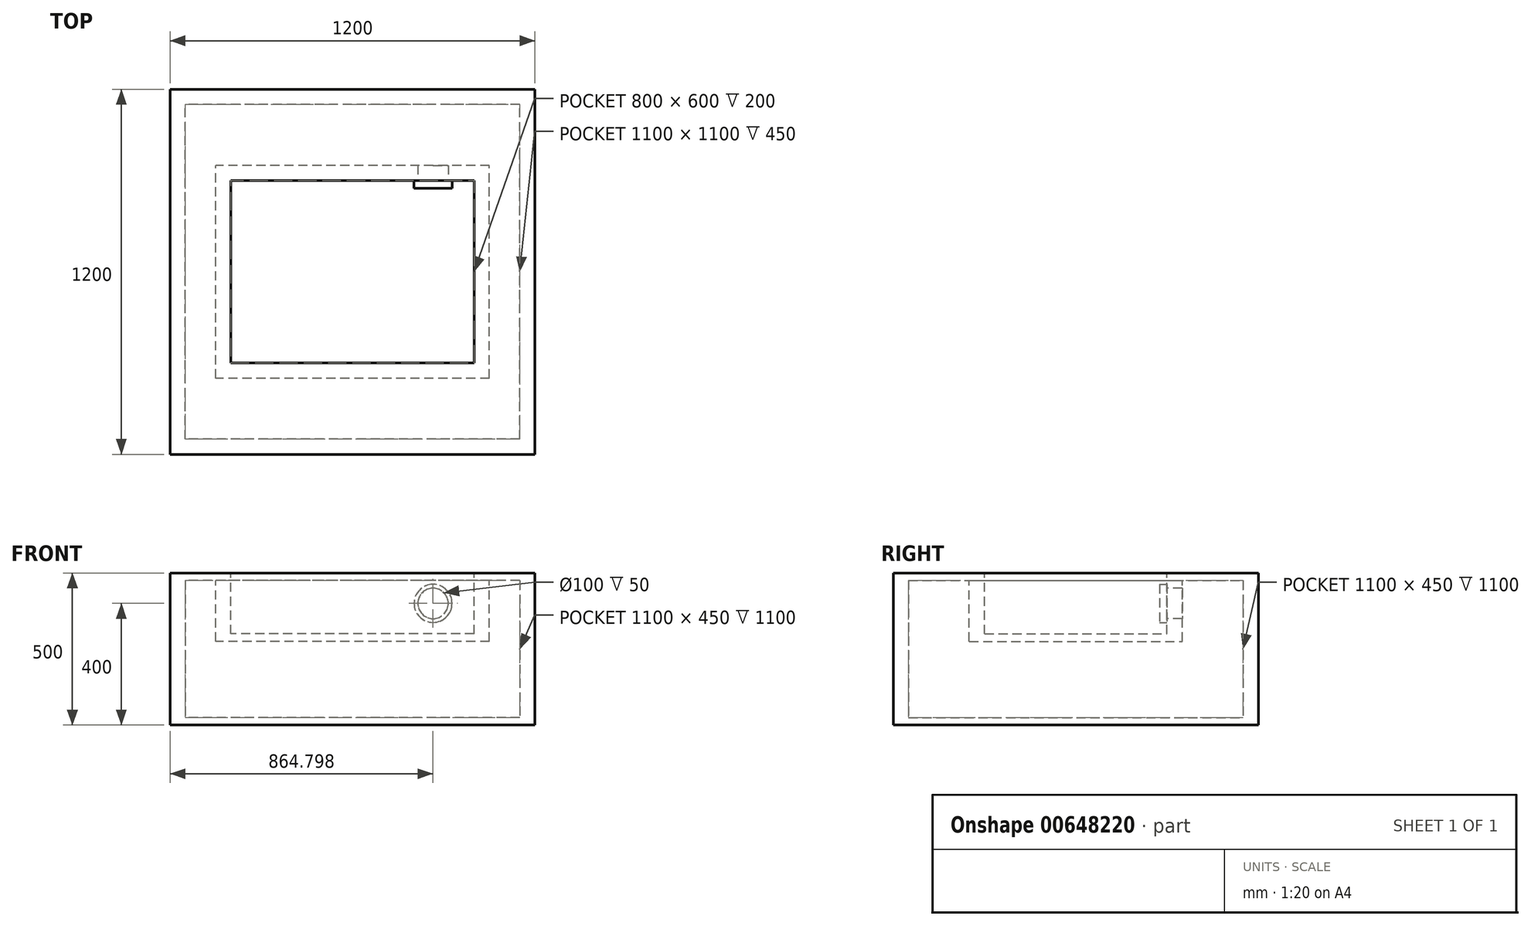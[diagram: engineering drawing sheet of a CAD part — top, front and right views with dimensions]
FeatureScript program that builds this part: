
annotation { "Feature Type Name" : "Feature", "Feature Type Description" : "" }
export const myFeature = defineFeature(function(context is Context, id is Id, definition is map)
    precondition{}
    {
        {
            var Q0;
            Q0=qCreatedBy(makeId("Top.planeOp"),FACE);
            var sketch = newSketch(context, id + "F0", { "sketchPlane" : qUnion([Q0])});
            skLineSegment(sketch, "E0.bottom", {"start": v(150, 150) * mm, "end": v(-150, 150) * mm, "construction": true});
            skLineSegment(sketch, "E0.top", {"start": v(150, -150) * mm, "end": v(-150, -150) * mm, "construction": true});
            skLineSegment(sketch, "E0.left", {"start": v(150, 150) * mm, "end": v(150, -150) * mm, "construction": true});
            skLineSegment(sketch, "E0.right", {"start": v(-150, 150) * mm, "end": v(-150, -150) * mm, "construction": true});
            skPoint(sketch, "E0.middle", {"position": v(0, 0) * mm});
            skPoint(sketch, "E1.0.1.0", {"position": v(0, 325) * mm});
            skLineSegment(sketch, "E1.0.1.1", {"start": v(-150, 475) * mm, "end": v(-150, 175) * mm, "construction": true});
            skLineSegment(sketch, "E1.0.1.2", {"start": v(150, 475) * mm, "end": v(150, 175) * mm, "construction": true});
            skLineSegment(sketch, "E1.0.1.3", {"start": v(150, 175) * mm, "end": v(-150, 175) * mm, "construction": true});
            skLineSegment(sketch, "E1.0.1.4", {"start": v(150, 475) * mm, "end": v(-150, 475) * mm, "construction": true});
            skLineSegment(sketch, "E1.0.2.1", {"start": v(-150, 800) * mm, "end": v(-150, 500) * mm, "construction": true});
            skLineSegment(sketch, "E1.0.2.2", {"start": v(150, 800) * mm, "end": v(150, 500) * mm, "construction": true});
            skLineSegment(sketch, "E1.0.2.3", {"start": v(150, 500) * mm, "end": v(-150, 500) * mm, "construction": true});
            skLineSegment(sketch, "E1.0.2.4", {"start": v(150, 800) * mm, "end": v(-150, 800) * mm, "construction": true});
            skPoint(sketch, "E1.1.0.0", {"position": v(325, 0) * mm});
            skLineSegment(sketch, "E1.1.0.1", {"start": v(175, 150) * mm, "end": v(175, -150) * mm, "construction": true});
            skLineSegment(sketch, "E1.1.0.2", {"start": v(475, 150) * mm, "end": v(475, -150) * mm, "construction": true});
            skLineSegment(sketch, "E1.1.0.3", {"start": v(475, -150) * mm, "end": v(175, -150) * mm, "construction": true});
            skLineSegment(sketch, "E1.1.0.4", {"start": v(475, 150) * mm, "end": v(175, 150) * mm, "construction": true});
            skPoint(sketch, "E1.1.1.0", {"position": v(325, 325) * mm});
            skLineSegment(sketch, "E1.1.1.1", {"start": v(175, 475) * mm, "end": v(175, 175) * mm, "construction": true});
            skLineSegment(sketch, "E1.1.1.2", {"start": v(475, 475) * mm, "end": v(475, 175) * mm, "construction": true});
            skLineSegment(sketch, "E1.1.1.3", {"start": v(475, 175) * mm, "end": v(175, 175) * mm, "construction": true});
            skLineSegment(sketch, "E1.1.1.4", {"start": v(475, 475) * mm, "end": v(175, 475) * mm, "construction": true});
            skPoint(sketch, "E1.1.2.0", {"position": v(325, 650) * mm});
            skLineSegment(sketch, "E1.1.2.1", {"start": v(175, 800) * mm, "end": v(175, 500) * mm, "construction": true});
            skLineSegment(sketch, "E1.1.2.2", {"start": v(475, 800) * mm, "end": v(475, 500) * mm, "construction": true});
            skLineSegment(sketch, "E1.1.2.3", {"start": v(475, 500) * mm, "end": v(175, 500) * mm, "construction": true});
            skLineSegment(sketch, "E1.1.2.4", {"start": v(475, 800) * mm, "end": v(175, 800) * mm, "construction": true});
            skLineSegment(sketch, "E1.2.0.1", {"start": v(500, 150) * mm, "end": v(500, -150) * mm, "construction": true});
            skLineSegment(sketch, "E1.2.0.2", {"start": v(800, 150) * mm, "end": v(800, -150) * mm, "construction": true});
            skLineSegment(sketch, "E1.2.0.3", {"start": v(800, -150) * mm, "end": v(500, -150) * mm, "construction": true});
            skLineSegment(sketch, "E1.2.0.4", {"start": v(800, 150) * mm, "end": v(500, 150) * mm, "construction": true});
            skPoint(sketch, "E1.2.1.0", {"position": v(650, 325) * mm});
            skLineSegment(sketch, "E1.2.1.1", {"start": v(500, 475) * mm, "end": v(500, 175) * mm, "construction": true});
            skLineSegment(sketch, "E1.2.1.2", {"start": v(800, 475) * mm, "end": v(800, 175) * mm, "construction": true});
            skLineSegment(sketch, "E1.2.1.3", {"start": v(800, 175) * mm, "end": v(500, 175) * mm, "construction": true});
            skLineSegment(sketch, "E1.2.1.4", {"start": v(800, 475) * mm, "end": v(500, 475) * mm, "construction": true});
            skLineSegment(sketch, "E1.2.2.1", {"start": v(500, 800) * mm, "end": v(500, 500) * mm, "construction": true});
            skLineSegment(sketch, "E1.2.2.2", {"start": v(800, 800) * mm, "end": v(800, 500) * mm, "construction": true});
            skLineSegment(sketch, "E1.2.2.3", {"start": v(800, 500) * mm, "end": v(500, 500) * mm, "construction": true});
            skLineSegment(sketch, "E1.2.2.4", {"start": v(800, 800) * mm, "end": v(500, 800) * mm, "construction": true});
            skLineSegment(sketch, "E1.direction1", {"start": v(-150, -150) * mm, "end": v(175, -150) * mm, "construction": true});
            skLineSegment(sketch, "E1.direction2", {"start": v(-150, -150) * mm, "end": v(-150, 175) * mm, "construction": true});
            skLineSegment(sketch, "E2", {"start": v(190, 425.96) * mm, "end": v(190, 175.96) * mm});
            skLineSegment(sketch, "E3", {"start": v(190, 175.96) * mm, "end": v(580, 175.96) * mm});
            skLineSegment(sketch, "E4", {"start": v(325, 350) * mm, "end": v(275, 350) * mm});
            skLineSegment(sketch, "E5", {"start": v(275, 350) * mm, "end": v(275, 275) * mm});
            skLineSegment(sketch, "E6", {"start": v(415, 275) * mm, "end": v(415, 425) * mm});
            skLineSegment(sketch, "E7", {"start": v(275, 275) * mm, "end": v(415, 275) * mm});
            skLineSegment(sketch, "E8", {"start": v(415, 425) * mm, "end": v(190, 425.96) * mm});
            skLineSegment(sketch, "E9", {"start": v(325, 350) * mm, "end": v(325, 300) * mm, "construction": true});
            skLineSegment(sketch, "E10", {"start": v(325, 300) * mm, "end": v(375, 300) * mm});
            skLineSegment(sketch, "E11", {"start": v(375, 300) * mm, "end": v(375, 375) * mm});
            skLineSegment(sketch, "E12", {"start": v(375, 375) * mm, "end": v(235, 375) * mm});
            skLineSegment(sketch, "E13", {"start": v(235, 375) * mm, "end": v(235, 225) * mm});
            skLineSegment(sketch, "E14", {"start": v(235, 225) * mm, "end": v(460, 225) * mm});
            skLineSegment(sketch, "E15", {"start": v(460, 225) * mm, "end": v(460, 475) * mm});
            skLineSegment(sketch, "E16", {"start": v(460, 475) * mm, "end": v(70, 475) * mm});
            skLineSegment(sketch, "E17.0", {"start": v(465, 480) * mm, "end": v(70, 480) * mm});
            skLineSegment(sketch, "E17.1", {"start": v(465, 220) * mm, "end": v(465, 480) * mm});
            skLineSegment(sketch, "E17.2", {"start": v(230, 220) * mm, "end": v(465, 220) * mm});
            skLineSegment(sketch, "E17.3", {"start": v(325, 295) * mm, "end": v(380, 295) * mm});
            skLineSegment(sketch, "E17.4", {"start": v(380, 295) * mm, "end": v(380, 380) * mm});
            skLineSegment(sketch, "E17.5", {"start": v(380, 380) * mm, "end": v(230, 380) * mm});
            skLineSegment(sketch, "E17.6", {"start": v(230, 380) * mm, "end": v(230, 220) * mm});
            skLineSegment(sketch, "E18", {"start": v(70, 480) * mm, "end": v(70, 475) * mm});
            skLineSegment(sketch, "E19", {"start": v(325, 300) * mm, "end": v(325, 295) * mm});
            skLineSegment(sketch, "E20.0", {"start": v(185, 170.96) * mm, "end": v(580, 170.96) * mm});
            skLineSegment(sketch, "E20.1", {"start": v(185, 430.98) * mm, "end": v(185, 170.96) * mm});
            skLineSegment(sketch, "E20.2", {"start": v(420, 429.98) * mm, "end": v(185, 430.98) * mm});
            skLineSegment(sketch, "E20.3", {"start": v(325, 355) * mm, "end": v(270, 355) * mm});
            skLineSegment(sketch, "E20.4", {"start": v(270, 355) * mm, "end": v(270, 270) * mm});
            skLineSegment(sketch, "E20.5", {"start": v(270, 270) * mm, "end": v(420, 270) * mm});
            skLineSegment(sketch, "E20.6", {"start": v(420, 270) * mm, "end": v(420, 429.98) * mm});
            skLineSegment(sketch, "E21", {"start": v(580, 175.96) * mm, "end": v(580, 170.96) * mm});
            skLineSegment(sketch, "E22", {"start": v(325, 355) * mm, "end": v(325, 350) * mm});
            skLineSegment(sketch, "E23", {"start": v(125, 75) * mm, "end": v(125, 150) * mm});
            skLineSegment(sketch, "E24", {"start": v(75, 150) * mm, "end": v(75, 50) * mm});
            skLineSegment(sketch, "E25", {"start": v(75, 50) * mm, "end": v(-75, 50) * mm});
            skLineSegment(sketch, "E26", {"start": v(-75, 50) * mm, "end": v(-75, -25) * mm});
            skLineSegment(sketch, "E27", {"start": v(-75, -25) * mm, "end": v(75, -25) * mm});
            skLineSegment(sketch, "E28", {"start": v(75, -25) * mm, "end": v(75, 0) * mm});
            skLineSegment(sketch, "E29", {"start": v(75, 0) * mm, "end": v(150, 0) * mm});
            skLineSegment(sketch, "E30", {"start": v(175, -75) * mm, "end": v(475, -75) * mm});
            skLineSegment(sketch, "E31", {"start": v(125, 75) * mm, "end": v(150, 75) * mm});
            skLineSegment(sketch, "E32", {"start": v(150, -75) * mm, "end": v(-115, -75) * mm});
            skLineSegment(sketch, "E33", {"start": v(-115, -75) * mm, "end": v(-115, 90) * mm});
            skLineSegment(sketch, "E34", {"start": v(-115, 90) * mm, "end": v(0, 90) * mm});
            skLineSegment(sketch, "E35", {"start": v(0, 90) * mm, "end": v(0, 150) * mm});
            skLineSegment(sketch, "E36", {"start": v(175, 0) * mm, "end": v(475, 0) * mm});
            skLineSegment(sketch, "E37", {"start": v(175, 75) * mm, "end": v(475, 75) * mm});
            skLineSegment(sketch, "E38", {"start": v(325, 150) * mm, "end": v(325, -150) * mm, "construction": true});
            skLineSegment(sketch, "E39.0", {"start": v(120, 70) * mm, "end": v(150, 70) * mm});
            skLineSegment(sketch, "E39.1", {"start": v(120, 70) * mm, "end": v(120, 150) * mm});
            skLineSegment(sketch, "E40.0", {"start": v(80, -5) * mm, "end": v(150, -5) * mm});
            skLineSegment(sketch, "E40.1", {"start": v(80, -30) * mm, "end": v(80, -5) * mm});
            skLineSegment(sketch, "E40.2", {"start": v(70, 150) * mm, "end": v(70, 55) * mm});
            skLineSegment(sketch, "E40.3", {"start": v(70, 55) * mm, "end": v(-80, 55) * mm});
            skLineSegment(sketch, "E40.4", {"start": v(-80, 55) * mm, "end": v(-80, -30) * mm});
            skLineSegment(sketch, "E40.5", {"start": v(-80, -30) * mm, "end": v(80, -30) * mm});
            skLineSegment(sketch, "E41.0", {"start": v(5, 85) * mm, "end": v(5, 150) * mm});
            skLineSegment(sketch, "E41.1", {"start": v(-110, 85) * mm, "end": v(5, 85) * mm});
            skLineSegment(sketch, "E41.2", {"start": v(-110, -70) * mm, "end": v(-110, 85) * mm});
            skLineSegment(sketch, "E41.3", {"start": v(150, -70) * mm, "end": v(-110, -70) * mm});
            skLineSegment(sketch, "E42.0", {"start": v(175, 70) * mm, "end": v(475, 70) * mm});
            skLineSegment(sketch, "E43.0", {"start": v(175, -5) * mm, "end": v(475, -5) * mm});
            skLineSegment(sketch, "E44.0", {"start": v(175, -70) * mm, "end": v(475, -70) * mm});
            skLineSegment(sketch, "E45", {"start": v(0, 175) * mm, "end": v(0, 475) * mm});
            skLineSegment(sketch, "E46", {"start": v(-75, 175) * mm, "end": v(-75, 475) * mm});
            skLineSegment(sketch, "E47", {"start": v(175, 75) * mm, "end": v(150, 75) * mm});
            skLineSegment(sketch, "E48", {"start": v(175, 70) * mm, "end": v(150, 70) * mm});
            skLineSegment(sketch, "E49", {"start": v(175, 0) * mm, "end": v(150, 0) * mm});
            skLineSegment(sketch, "E50", {"start": v(175, -5) * mm, "end": v(150, -5) * mm});
            skLineSegment(sketch, "E51", {"start": v(175, -70) * mm, "end": v(150, -70) * mm});
            skLineSegment(sketch, "E52", {"start": v(175, -75) * mm, "end": v(150, -75) * mm});
            skLineSegment(sketch, "E53.0", {"start": v(5, 175) * mm, "end": v(5, 475) * mm});
            skLineSegment(sketch, "E54", {"start": v(5, 150) * mm, "end": v(5, 175) * mm});
            skLineSegment(sketch, "E55", {"start": v(70, 150) * mm, "end": v(70, 175) * mm});
            skLineSegment(sketch, "E56", {"start": v(75, 150) * mm, "end": v(75, 175) * mm});
            skLineSegment(sketch, "E57", {"start": v(120, 150) * mm, "end": v(120, 175) * mm});
            skLineSegment(sketch, "E58", {"start": v(125, 150) * mm, "end": v(125, 175) * mm});
            skLineSegment(sketch, "E59.MirrorCS", {"start": v(475, -75) * mm, "end": v(500, -75) * mm});
            skLineSegment(sketch, "E60.MirrorCS", {"start": v(475, -70) * mm, "end": v(500, -70) * mm});
            skLineSegment(sketch, "E61.MirrorCS", {"start": v(475, 70) * mm, "end": v(500, 70) * mm});
            skLineSegment(sketch, "E62.MirrorCS", {"start": v(475, -5) * mm, "end": v(500, -5) * mm});
            skLineSegment(sketch, "E63.MirrorCS", {"start": v(475, 75) * mm, "end": v(500, 75) * mm});
            skLineSegment(sketch, "E64.MirrorCS", {"start": v(475, 0) * mm, "end": v(500, 0) * mm});
            skLineSegment(sketch, "E65", {"start": v(500, 70) * mm, "end": v(575, 70) * mm});
            skLineSegment(sketch, "E66", {"start": v(575, 70) * mm, "end": v(575, -30) * mm});
            skLineSegment(sketch, "E67", {"start": v(575, -30) * mm, "end": v(725, -30) * mm});
            skLineSegment(sketch, "E68", {"start": v(725, -30) * mm, "end": v(725, 45) * mm});
            skLineSegment(sketch, "E69", {"start": v(725, 45) * mm, "end": v(650, 45) * mm});
            skLineSegment(sketch, "E70", {"start": v(650, 45) * mm, "end": v(650, 150) * mm});
            skLineSegment(sketch, "E71", {"start": v(500, -5) * mm, "end": v(535, -5) * mm});
            skLineSegment(sketch, "E72", {"start": v(535, -5) * mm, "end": v(535, -80) * mm});
            skLineSegment(sketch, "E73", {"start": v(535, -80) * mm, "end": v(760, -80) * mm});
            skLineSegment(sketch, "E74", {"start": v(760, -80) * mm, "end": v(760, 115) * mm});
            skLineSegment(sketch, "E75", {"start": v(760, 115) * mm, "end": v(725, 115) * mm});
            skLineSegment(sketch, "E76", {"start": v(725, 115) * mm, "end": v(725, 150) * mm});
            skLineSegment(sketch, "E77", {"start": v(500, -75) * mm, "end": v(513.03, -75) * mm});
            skLineSegment(sketch, "E78", {"start": v(513.03, -75) * mm, "end": v(513.03, -95) * mm});
            skLineSegment(sketch, "E79", {"start": v(513.03, -95) * mm, "end": v(763.03, -95) * mm});
            skLineSegment(sketch, "E80.0", {"start": v(518.03, -90) * mm, "end": v(763.03, -90) * mm});
            skLineSegment(sketch, "E80.1", {"start": v(518.03, -70) * mm, "end": v(518.03, -90) * mm});
            skLineSegment(sketch, "E80.2", {"start": v(500, -70) * mm, "end": v(518.03, -70) * mm});
            skLineSegment(sketch, "E81.0", {"start": v(645, 40) * mm, "end": v(645, 150) * mm});
            skLineSegment(sketch, "E81.1", {"start": v(720, 40) * mm, "end": v(645, 40) * mm});
            skLineSegment(sketch, "E81.2", {"start": v(500, 75) * mm, "end": v(580, 75) * mm});
            skLineSegment(sketch, "E81.3", {"start": v(580, 75) * mm, "end": v(580, -25) * mm});
            skLineSegment(sketch, "E81.4", {"start": v(580, -25) * mm, "end": v(720, -25) * mm});
            skLineSegment(sketch, "E81.5", {"start": v(720, -25) * mm, "end": v(720, 40) * mm});
            skLineSegment(sketch, "E82.0", {"start": v(720, 110) * mm, "end": v(720, 150) * mm});
            skLineSegment(sketch, "E82.1", {"start": v(755, 110) * mm, "end": v(720, 110) * mm});
            skLineSegment(sketch, "E82.2", {"start": v(500, 0) * mm, "end": v(540, 0) * mm});
            skLineSegment(sketch, "E82.3", {"start": v(540, 0) * mm, "end": v(540, -75) * mm});
            skLineSegment(sketch, "E82.4", {"start": v(540, -75) * mm, "end": v(755, -75) * mm});
            skLineSegment(sketch, "E82.5", {"start": v(755, -75) * mm, "end": v(755, 110) * mm});
            skLineSegment(sketch, "E83", {"start": v(650, 175) * mm, "end": v(650, 475) * mm});
            skLineSegment(sketch, "E84", {"start": v(725, 175) * mm, "end": v(725, 475) * mm});
            skLineSegment(sketch, "E85.0", {"start": v(645, 175) * mm, "end": v(645, 475) * mm});
            skLineSegment(sketch, "E86.0", {"start": v(720, 175) * mm, "end": v(720, 475) * mm});
            skLineSegment(sketch, "E87", {"start": v(650, 150) * mm, "end": v(650, 175) * mm});
            skLineSegment(sketch, "E88", {"start": v(645, 150) * mm, "end": v(645, 175) * mm});
            skLineSegment(sketch, "E89", {"start": v(725, 150) * mm, "end": v(725, 175) * mm});
            skLineSegment(sketch, "E90", {"start": v(720, 150) * mm, "end": v(720, 175) * mm});
            skLineSegment(sketch, "E91", {"start": v(525, 475) * mm, "end": v(525, 235) * mm});
            skLineSegment(sketch, "E92", {"start": v(575, 475) * mm, "end": v(575, 240) * mm});
            skLineSegment(sketch, "E93", {"start": v(150, 325) * mm, "end": v(-150, 325) * mm, "construction": true});
            skLineSegment(sketch, "E94.0", {"start": v(580, 475) * mm, "end": v(580, 235) * mm});
            skLineSegment(sketch, "E95.0", {"start": v(530, 475) * mm, "end": v(530, 240) * mm});
            skLineSegment(sketch, "E96", {"start": v(763.03, -90) * mm, "end": v(763.03, -95) * mm});
            skLineSegment(sketch, "E97.MirrorCS", {"start": v(-113.03, 740) * mm, "end": v(-113.03, 745) * mm});
            skLineSegment(sketch, "E98.MirrorCS", {"start": v(150, 725) * mm, "end": v(136.97, 725) * mm});
            skLineSegment(sketch, "E99.MirrorCS", {"start": v(150, 720) * mm, "end": v(131.97, 720) * mm});
            skLineSegment(sketch, "E100.MirrorCS", {"start": v(-105, 725) * mm, "end": v(-105, 540) * mm});
            skLineSegment(sketch, "E101.MirrorCS", {"start": v(150, 580) * mm, "end": v(75, 580) * mm});
            skLineSegment(sketch, "E102.MirrorCS", {"start": v(136.97, 745) * mm, "end": v(-113.03, 745) * mm});
            skLineSegment(sketch, "E103.MirrorCS", {"start": v(-70, 675) * mm, "end": v(-70, 610) * mm});
            skLineSegment(sketch, "E104.MirrorCS", {"start": v(-110, 730) * mm, "end": v(-110, 535) * mm});
            skLineSegment(sketch, "E105.MirrorCS", {"start": v(-70, 540) * mm, "end": v(-70, 500) * mm});
            skLineSegment(sketch, "E106.MirrorCS", {"start": v(-75, 605) * mm, "end": v(0, 605) * mm});
            skLineSegment(sketch, "E107.MirrorCS", {"start": v(70, 575) * mm, "end": v(70, 675) * mm});
            skLineSegment(sketch, "E108.MirrorCS", {"start": v(-75, 535) * mm, "end": v(-75, 500) * mm});
            skLineSegment(sketch, "E109.MirrorCS", {"start": v(-105, 540) * mm, "end": v(-70, 540) * mm});
            skLineSegment(sketch, "E110.MirrorCS", {"start": v(-70, 610) * mm, "end": v(5, 610) * mm});
            skLineSegment(sketch, "E111.MirrorCS", {"start": v(5, 610) * mm, "end": v(5, 500) * mm});
            skLineSegment(sketch, "E112.MirrorCS", {"start": v(70, 675) * mm, "end": v(-70, 675) * mm});
            skLineSegment(sketch, "E113.MirrorCS", {"start": v(115, 730) * mm, "end": v(-110, 730) * mm});
            skLineSegment(sketch, "E114.MirrorCS", {"start": v(131.97, 740) * mm, "end": v(-113.03, 740) * mm});
            skLineSegment(sketch, "E115.MirrorCS", {"start": v(150, 655) * mm, "end": v(115, 655) * mm});
            skLineSegment(sketch, "E116.MirrorCS", {"start": v(110, 650) * mm, "end": v(110, 725) * mm});
            skLineSegment(sketch, "E117.MirrorCS", {"start": v(150, 575) * mm, "end": v(70, 575) * mm});
            skLineSegment(sketch, "E118.MirrorCS", {"start": v(-110, 535) * mm, "end": v(-75, 535) * mm});
            skLineSegment(sketch, "E119.MirrorCS", {"start": v(75, 580) * mm, "end": v(75, 680) * mm});
            skLineSegment(sketch, "E120.MirrorCS", {"start": v(136.97, 725) * mm, "end": v(136.97, 745) * mm});
            skLineSegment(sketch, "E121.MirrorCS", {"start": v(115, 655) * mm, "end": v(115, 730) * mm});
            skLineSegment(sketch, "E122.MirrorCS", {"start": v(131.97, 720) * mm, "end": v(131.97, 740) * mm});
            skLineSegment(sketch, "E123.MirrorCS", {"start": v(110, 725) * mm, "end": v(-105, 725) * mm});
            skLineSegment(sketch, "E124.MirrorCS", {"start": v(-75, 680) * mm, "end": v(-75, 605) * mm});
            skLineSegment(sketch, "E125.MirrorCS", {"start": v(0, 605) * mm, "end": v(0, 500) * mm});
            skLineSegment(sketch, "E126.MirrorCS", {"start": v(150, 650) * mm, "end": v(110, 650) * mm});
            skLineSegment(sketch, "E127.MirrorCS", {"start": v(75, 680) * mm, "end": v(-75, 680) * mm});
            skPoint(sketch, "E128.2.2.0", {"position": v(650, 650) * mm});
            skLineSegment(sketch, "E129.MirrorCS", {"start": v(570, 680) * mm, "end": v(570, 655) * mm});
            skLineSegment(sketch, "E130.MirrorCS", {"start": v(575, 675) * mm, "end": v(575, 650) * mm});
            skLineSegment(sketch, "E131.MirrorCS", {"start": v(525, 575) * mm, "end": v(500, 575) * mm});
            skLineSegment(sketch, "E132.MirrorCS", {"start": v(570, 655) * mm, "end": v(500, 655) * mm});
            skLineSegment(sketch, "E133.MirrorCS", {"start": v(530, 580) * mm, "end": v(500, 580) * mm});
            skLineSegment(sketch, "E134.MirrorCS", {"start": v(580, 595) * mm, "end": v(730, 595) * mm});
            skLineSegment(sketch, "E135.MirrorCS", {"start": v(730, 595) * mm, "end": v(730, 680) * mm});
            skLineSegment(sketch, "E136.MirrorCS", {"start": v(650, 560) * mm, "end": v(650, 500) * mm});
            skLineSegment(sketch, "E137.MirrorCS", {"start": v(580, 500) * mm, "end": v(580, 595) * mm});
            skLineSegment(sketch, "E138.MirrorCS", {"start": v(645, 565) * mm, "end": v(645, 500) * mm});
            skLineSegment(sketch, "E139.MirrorCS", {"start": v(760, 565) * mm, "end": v(645, 565) * mm});
            skLineSegment(sketch, "E140.MirrorCS", {"start": v(575, 600) * mm, "end": v(725, 600) * mm});
            skLineSegment(sketch, "E141.MirrorCS", {"start": v(575, 650) * mm, "end": v(500, 650) * mm});
            skLineSegment(sketch, "E142.MirrorCS", {"start": v(730, 680) * mm, "end": v(570, 680) * mm});
            skLineSegment(sketch, "E143.MirrorCS", {"start": v(500, 720) * mm, "end": v(760, 720) * mm});
            skLineSegment(sketch, "E144.MirrorCS", {"start": v(765, 560) * mm, "end": v(650, 560) * mm});
            skLineSegment(sketch, "E145.MirrorCS", {"start": v(575, 500) * mm, "end": v(575, 600) * mm});
            skLineSegment(sketch, "E146.MirrorCS", {"start": v(525, 575) * mm, "end": v(525, 500) * mm});
            skLineSegment(sketch, "E147.MirrorCS", {"start": v(760, 720) * mm, "end": v(760, 565) * mm});
            skLineSegment(sketch, "E148.MirrorCS", {"start": v(765, 725) * mm, "end": v(765, 560) * mm});
            skLineSegment(sketch, "E149.MirrorCS", {"start": v(725, 675) * mm, "end": v(575, 675) * mm});
            skLineSegment(sketch, "E150.MirrorCS", {"start": v(500, 725) * mm, "end": v(765, 725) * mm});
            skLineSegment(sketch, "E151.MirrorCS", {"start": v(725, 600) * mm, "end": v(725, 675) * mm});
            skLineSegment(sketch, "E152.MirrorCS", {"start": v(530, 580) * mm, "end": v(530, 500) * mm});
            skLineSegment(sketch, "E153.MirrorCS", {"start": v(175, 725) * mm, "end": v(475, 725) * mm});
            skLineSegment(sketch, "E154.MirrorCS", {"start": v(175, 720) * mm, "end": v(475, 720) * mm});
            skLineSegment(sketch, "E155.MirrorCS", {"start": v(175, 655) * mm, "end": v(475, 655) * mm});
            skLineSegment(sketch, "E156.MirrorCS", {"start": v(175, 650) * mm, "end": v(475, 650) * mm});
            skLineSegment(sketch, "E157.MirrorCS", {"start": v(175, 575) * mm, "end": v(475, 575) * mm});
            skLineSegment(sketch, "E158.MirrorCS", {"start": v(175, 580) * mm, "end": v(475, 580) * mm});
            skLineSegment(sketch, "E159", {"start": v(150, 725) * mm, "end": v(175, 725) * mm});
            skLineSegment(sketch, "E160", {"start": v(150, 720) * mm, "end": v(175, 720) * mm});
            skLineSegment(sketch, "E161", {"start": v(150, 655) * mm, "end": v(175, 655) * mm});
            skLineSegment(sketch, "E162", {"start": v(150, 650) * mm, "end": v(175, 650) * mm});
            skLineSegment(sketch, "E163", {"start": v(150, 580) * mm, "end": v(175, 580) * mm});
            skLineSegment(sketch, "E164", {"start": v(150, 575) * mm, "end": v(175, 575) * mm});
            skLineSegment(sketch, "E165", {"start": v(475, 725) * mm, "end": v(500, 725) * mm});
            skLineSegment(sketch, "E166", {"start": v(475, 720) * mm, "end": v(500, 720) * mm});
            skLineSegment(sketch, "E167", {"start": v(475, 655) * mm, "end": v(500, 655) * mm});
            skLineSegment(sketch, "E168", {"start": v(475, 650) * mm, "end": v(500, 650) * mm});
            skLineSegment(sketch, "E169", {"start": v(475, 580) * mm, "end": v(500, 580) * mm});
            skLineSegment(sketch, "E170", {"start": v(475, 575) * mm, "end": v(500, 575) * mm});
            skLineSegment(sketch, "E171", {"start": v(530, 500) * mm, "end": v(530, 475) * mm});
            skLineSegment(sketch, "E172", {"start": v(525, 500) * mm, "end": v(525, 475) * mm});
            skLineSegment(sketch, "E173", {"start": v(580, 500) * mm, "end": v(580, 475) * mm});
            skLineSegment(sketch, "E174", {"start": v(575, 500) * mm, "end": v(575, 475) * mm});
            skLineSegment(sketch, "E175", {"start": v(650, 500) * mm, "end": v(650, 475) * mm});
            skLineSegment(sketch, "E176", {"start": v(645, 500) * mm, "end": v(645, 475) * mm});
            skLineSegment(sketch, "E177", {"start": v(5, 475) * mm, "end": v(5, 500) * mm});
            skLineSegment(sketch, "E178", {"start": v(0, 475) * mm, "end": v(0, 500) * mm});
            skLineSegment(sketch, "E179.0", {"start": v(-70, 175) * mm, "end": v(-70, 475) * mm});
            skLineSegment(sketch, "E180", {"start": v(-75, 500) * mm, "end": v(-75, 475) * mm});
            skLineSegment(sketch, "E181", {"start": v(-70, 500) * mm, "end": v(-70, 475) * mm});
            skLineSegment(sketch, "E182", {"start": v(530, 240) * mm, "end": v(575, 240) * mm});
            skLineSegment(sketch, "E183", {"start": v(525, 235) * mm, "end": v(580, 235) * mm});
            skLineSegment(sketch, "E184", {"start": v(70, 175) * mm, "end": v(70, 415) * mm});
            skLineSegment(sketch, "E185", {"start": v(75, 175) * mm, "end": v(75, 410) * mm});
            skLineSegment(sketch, "E186", {"start": v(125, 175) * mm, "end": v(125, 415) * mm});
            skLineSegment(sketch, "E187", {"start": v(120, 175) * mm, "end": v(120, 410) * mm});
            skLineSegment(sketch, "E188", {"start": v(70, 415) * mm, "end": v(125, 415) * mm});
            skLineSegment(sketch, "E189", {"start": v(75, 410) * mm, "end": v(120, 410) * mm});
            skLineSegment(sketch, "E190", {"start": v(0, 175) * mm, "end": v(0, 150) * mm});
            skLineSegment(sketch, "E191", {"start": v(-70, 175) * mm, "end": v(-75, 175) * mm});
            skLineSegment(sketch, "E192", {"start": v(725, 475) * mm, "end": v(720, 475) * mm});
            skLineSegment(sketch, "E193.bottom", {"start": v(-150, 800) * mm, "end": v(800, 800) * mm});
            skLineSegment(sketch, "E193.top", {"start": v(-150, -150) * mm, "end": v(800, -150) * mm});
            skLineSegment(sketch, "E193.left", {"start": v(-150, 800) * mm, "end": v(-150, -150) * mm});
            skLineSegment(sketch, "E193.right", {"start": v(800, 800) * mm, "end": v(800, -150) * mm});
            skLineSegment(sketch, "E194.bottom", {"start": v(925, -275) * mm, "end": v(-275, -275) * mm});
            skLineSegment(sketch, "E194.top", {"start": v(925, 925) * mm, "end": v(-275, 925) * mm});
            skLineSegment(sketch, "E194.left", {"start": v(925, -275) * mm, "end": v(925, 925) * mm});
            skLineSegment(sketch, "E194.right", {"start": v(-275, -275) * mm, "end": v(-275, 925) * mm});
            skLineSegment(sketch, "E195.0", {"start": v(875, -225) * mm, "end": v(-225, -225) * mm});
            skLineSegment(sketch, "E195.1", {"start": v(875, -225) * mm, "end": v(875, 875) * mm});
            skLineSegment(sketch, "E195.2", {"start": v(875, 875) * mm, "end": v(-225, 875) * mm});
            skLineSegment(sketch, "E195.3", {"start": v(-225, -225) * mm, "end": v(-225, 875) * mm});
            skSolve(sketch);
        }
        {
            var Q0;
            Q0=makeQuery(id+"F0.imprint","IMPRINT",FACE,{"disambiguationData":[TD([[makeQuery(id+"F0.imprint","IMPRINT",EDGE,{"derivedFrom":sQuery(id+"F0.wireOp",EDGE,"E194.bottom")}),-1.0]])]});
            extrude(context, id + "F1", {"entities" : qUnion([Q0]), "depth" : 450 * mm, "offsetDistance" : 25 * mm});
        }
        {
            var Q0;
            Q0=makeQuery(id+"F1.opExtrude","CAP_FACE",FACE,{"disambiguationData":[OSD([sQuery(id+"F0.wireOp",EDGE,"E193.bottom"),sQuery(id+"F0.wireOp",EDGE,"E193.top"),sQuery(id+"F0.wireOp",EDGE,"E193.left"),sQuery(id+"F0.wireOp",EDGE,"E193.right"),sQuery(id+"F0.wireOp",EDGE,"E194.bottom"),sQuery(id+"F0.wireOp",EDGE,"E194.top"),sQuery(id+"F0.wireOp",EDGE,"E194.left"),sQuery(id+"F0.wireOp",EDGE,"E194.right")])],"isStart":false});
            var sketch = newSketch(context, id + "F2", { "sketchPlane" : qUnion([Q0])});
            skLineSegment(sketch, "E196.bottom", {"start": v(-275, -275) * mm, "end": v(925, -275) * mm});
            skLineSegment(sketch, "E196.top", {"start": v(-275, 925) * mm, "end": v(925, 925) * mm});
            skLineSegment(sketch, "E196.left", {"start": v(-275, -275) * mm, "end": v(-275, 925) * mm});
            skLineSegment(sketch, "E196.right", {"start": v(925, -275) * mm, "end": v(925, 925) * mm});
            skSolve(sketch);
        }
        {
            var Q0;
            Q0=makeQuery(id+"F2.imprint","IMPRINT",FACE,{"disambiguationData":[TD([[makeQuery(id+"F2.imprint","IMPRINT",EDGE,{"derivedFrom":sQuery(id+"F2.wireOp",EDGE,"E196.bottom")}),-1.0]])]});
            var Q1;
            Q1=makeQuery(id+"F2.imprint","IMPRINT",FACE,{"disambiguationData":[TD([[makeQuery(id+"F2.imprint","IMPRINT",EDGE,{"derivedFrom":makeQuery(id+"F1.opExtrude","CAP_EDGE",EDGE,{"disambiguationData":[OSD([sQuery(id+"F0.wireOp",EDGE,"E193.bottom")])],"isStart":false})}),-1.0]])]});
            var Q2;
            Q2=makeQuery(id+"F2.imprint","IMPRINT",FACE,{"disambiguationData":[TD([[makeQuery(id+"F2.imprint","IMPRINT",EDGE,{"derivedFrom":makeQuery(id+"F1.opExtrude","CAP_EDGE",EDGE,{"disambiguationData":[OSD([sQuery(id+"F0.wireOp",EDGE,"E195.0")])],"isStart":false})}),-1.0]])]});
            extrude(context, id + "F3", {"entities" : qUnion([Q0, Q1, Q2]), "operationType" : NewBodyOperationType.ADD, "depth" : 25 * mm, "offsetDistance" : 25 * mm});
        }
        {
            var Q0;
            Q0=makeQuery(id+"F3.opExtrude","CAP_FACE",FACE,{"disambiguationData":[OSD([sQuery(id+"F2.wireOp",EDGE,"E196.bottom"),sQuery(id+"F2.wireOp",EDGE,"E196.top"),sQuery(id+"F2.wireOp",EDGE,"E196.left"),sQuery(id+"F2.wireOp",EDGE,"E196.right")])],"isStart":true});
            var sketch = newSketch(context, id + "F4", { "sketchPlane" : qUnion([Q0])});
            skLineSegment(sketch, "E197.bottom", {"start": v(775, 25) * mm, "end": v(-125, 25) * mm});
            skLineSegment(sketch, "E197.top", {"start": v(775, -675) * mm, "end": v(-125, -675) * mm});
            skLineSegment(sketch, "E197.left", {"start": v(775, 25) * mm, "end": v(775, -675) * mm});
            skLineSegment(sketch, "E197.right", {"start": v(-125, 25) * mm, "end": v(-125, -675) * mm});
            skPoint(sketch, "E197.middle", {"position": v(325, -325) * mm});
            skSolve(sketch);
        }
        {
            var Q0;
            Q0=makeQuery(id+"F4.imprint","IMPRINT",FACE,{"disambiguationData":[TD([[makeQuery(id+"F4.imprint","IMPRINT",EDGE,{"derivedFrom":sQuery(id+"F4.wireOp",EDGE,"E197.bottom")}),1.0]])]});
            extrude(context, id + "F5", {"entities" : qUnion([Q0]), "operationType" : NewBodyOperationType.ADD, "depth" : 200 * mm, "offsetDistance" : 25 * mm});
        }
        {
            var Q0;
            Q0=makeQuery(id+"F1.opExtrude","CAP_FACE",FACE,{"disambiguationData":[OSD([sQuery(id+"F0.wireOp",EDGE,"E194.bottom"),sQuery(id+"F0.wireOp",EDGE,"E194.top"),sQuery(id+"F0.wireOp",EDGE,"E194.left"),sQuery(id+"F0.wireOp",EDGE,"E194.right"),sQuery(id+"F0.wireOp",EDGE,"E195.0"),sQuery(id+"F0.wireOp",EDGE,"E195.1"),sQuery(id+"F0.wireOp",EDGE,"E195.2"),sQuery(id+"F0.wireOp",EDGE,"E195.3")])],"isStart":true});
            var sketch = newSketch(context, id + "F6", { "sketchPlane" : qUnion([Q0])});
            skLineSegment(sketch, "E198.bottom", {"start": v(-275, 275) * mm, "end": v(925, 275) * mm});
            skLineSegment(sketch, "E198.top", {"start": v(-275, -925) * mm, "end": v(925, -925) * mm});
            skLineSegment(sketch, "E198.left", {"start": v(-275, 275) * mm, "end": v(-275, -925) * mm});
            skLineSegment(sketch, "E198.right", {"start": v(925, 275) * mm, "end": v(925, -925) * mm});
            skSolve(sketch);
        }
        {
            var Q0;
            Q0=makeQuery(id+"F6.imprint","IMPRINT",FACE,{"disambiguationData":[TD([[makeQuery(id+"F6.imprint","IMPRINT",EDGE,{"derivedFrom":sQuery(id+"F6.wireOp",EDGE,"E198.bottom")}),1.0]])]});
            var Q1;
            Q1=makeQuery(id+"F6.imprint","IMPRINT",FACE,{"disambiguationData":[TD([[makeQuery(id+"F6.imprint","IMPRINT",EDGE,{"derivedFrom":makeQuery(id+"F1.opExtrude","CAP_EDGE",EDGE,{"disambiguationData":[OSD([sQuery(id+"F0.wireOp",EDGE,"E195.0")])],"isStart":true})}),1.0]])]});
            extrude(context, id + "F7", {"entities" : qUnion([Q0, Q1]), "operationType" : NewBodyOperationType.ADD, "depth" : 25 * mm, "offsetDistance" : 25 * mm});
        }
        {
            var Q0;
            Q0=makeQuery(id+"F3.opExtrude","CAP_FACE",FACE,{"disambiguationData":[OSD([sQuery(id+"F2.wireOp",EDGE,"E196.bottom"),sQuery(id+"F2.wireOp",EDGE,"E196.top"),sQuery(id+"F2.wireOp",EDGE,"E196.left"),sQuery(id+"F2.wireOp",EDGE,"E196.right")])],"isStart":false});
            var sketch = newSketch(context, id + "F8", { "sketchPlane" : qUnion([Q0])});
            skLineSegment(sketch, "E199.bottom", {"start": v(725, 25) * mm, "end": v(-75, 25) * mm});
            skLineSegment(sketch, "E199.top", {"start": v(725, 625) * mm, "end": v(-75, 625) * mm});
            skLineSegment(sketch, "E199.left", {"start": v(725, 25) * mm, "end": v(725, 625) * mm});
            skLineSegment(sketch, "E199.right", {"start": v(-75, 25) * mm, "end": v(-75, 625) * mm});
            skPoint(sketch, "E199.middle", {"position": v(325, 325) * mm});
            skSolve(sketch);
        }
        {
            var Q0;
            Q0=makeQuery(id+"F8.imprint","IMPRINT",FACE,{"disambiguationData":[TD([[makeQuery(id+"F8.imprint","IMPRINT",EDGE,{"derivedFrom":sQuery(id+"F8.wireOp",EDGE,"E199.bottom")}),-1.0]])]});
            extrude(context, id + "F9", {"entities" : qUnion([Q0]), "operationType" : NewBodyOperationType.REMOVE, "oppositeDirection" : true, "depth" : 200 * mm, "offsetDistance" : 25 * mm});
        }
        {
            var Q0;
            Q0=makeQuery(id+"F9.boolean.opBoolean","COPY",FACE,{"derivedFrom":makeQuery(id+"F9.opExtrude","SWEPT_FACE",FACE,{"disambiguationData":[OSD([sQuery(id+"F8.wireOp",EDGE,"E199.top")])]})});
            var sketch = newSketch(context, id + "F10", { "sketchPlane" : qUnion([Q0])});
            skCircle(sketch, "E200", {"center": v(589.8, 375) * mm, "radius": 50 * mm});
            skSolve(sketch);
        }
        {
            var Q0;
            Q0=makeQuery(id+"F10.imprint","IMPRINT",FACE,{"disambiguationData":[TD([[makeQuery(id+"F10.imprint","IMPRINT",EDGE,{"derivedFrom":sQuery(id+"F10.wireOp",EDGE,"E200")}),1.0]])]});
            extrude(context, id + "F11", {"entities" : qUnion([Q0]), "operationType" : NewBodyOperationType.REMOVE, "endBound" : BoundingType.UP_TO_NEXT, "oppositeDirection" : true, "depth" : 25 * mm, "offsetDistance" : 25 * mm});
        }
        {
            var Q0;
            Q0=makeQuery(id+"F9.boolean.opBoolean","COPY",FACE,{"derivedFrom":makeQuery(id+"F9.opExtrude","SWEPT_FACE",FACE,{"disambiguationData":[OSD([sQuery(id+"F8.wireOp",EDGE,"E199.top")])]})});
            var sketch = newSketch(context, id + "F12", { "sketchPlane" : qUnion([Q0])});
            skCircle(sketch, "E201", {"center": v(589.8, 375) * mm, "radius": 50 * mm});
            skCircle(sketch, "E202", {"center": v(589.8, 375) * mm, "radius": 62.5 * mm});
            skSolve(sketch);
        }
        {
            var Q0;
            Q0=makeQuery(id+"F12.imprint","IMPRINT",FACE,{"disambiguationData":[TD([[makeQuery(id+"F12.imprint","IMPRINT",EDGE,{"derivedFrom":sQuery(id+"F12.wireOp",EDGE,"E201")}),-1.0]])]});
            var Q1;
            Q1=makeQuery(id+"F12.imprint","IMPRINT",FACE,{"disambiguationData":[TD([[makeQuery(id+"F12.imprint","IMPRINT",EDGE,{"derivedFrom":sQuery(id+"F12.wireOp",EDGE,"E201")}),1.0]])]});
            extrude(context, id + "F13", {"entities" : qUnion([Q0, Q1]), "operationType" : NewBodyOperationType.ADD, "depth" : 25 * mm, "offsetDistance" : 25 * mm});
        }
    });
